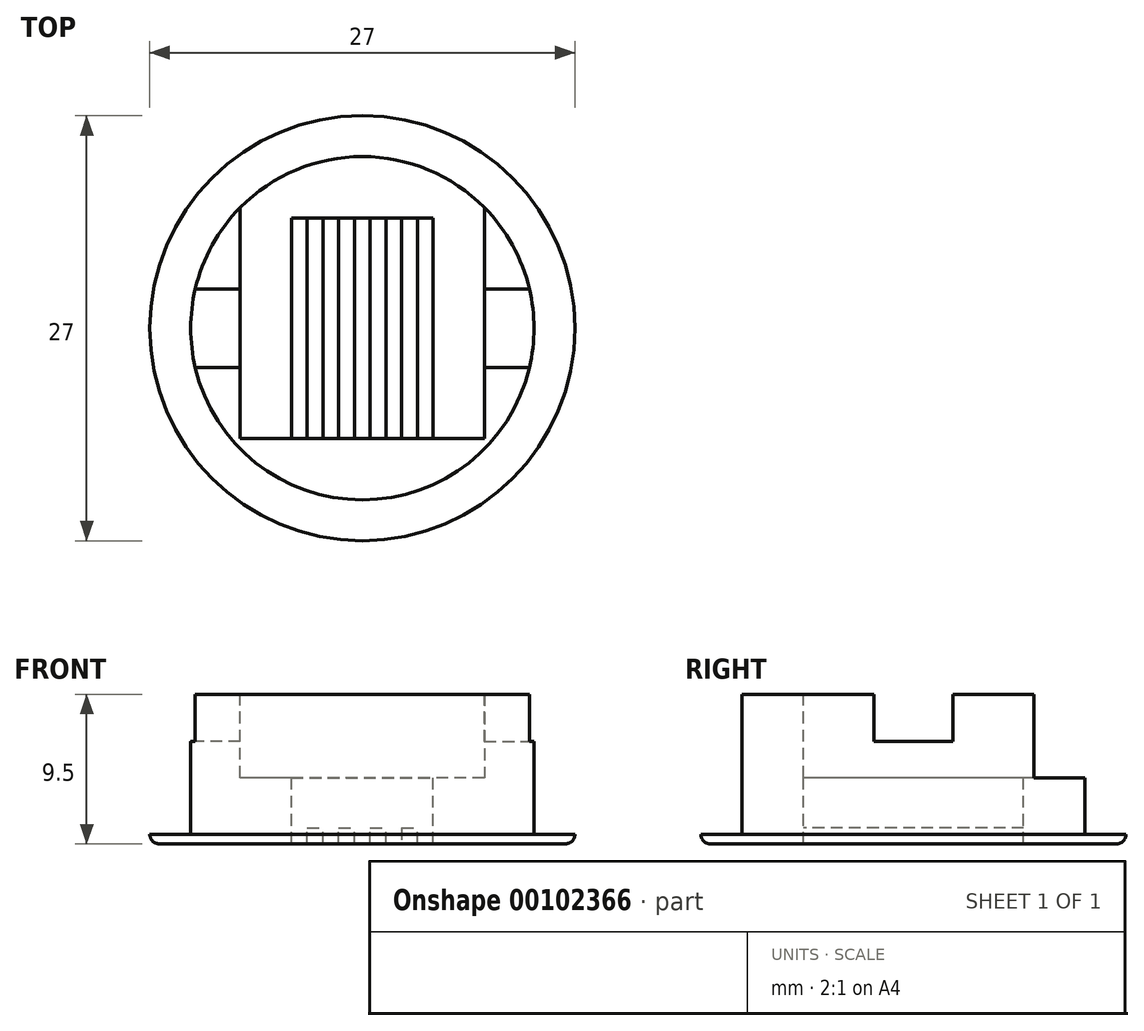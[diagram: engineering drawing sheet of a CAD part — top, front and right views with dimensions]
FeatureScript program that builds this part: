
annotation { "Feature Type Name" : "Feature", "Feature Type Description" : "" }
export const myFeature = defineFeature(function(context is Context, id is Id, definition is map)
    precondition{}
    {
        {
            var Q0;
            Q0=qCreatedBy(makeId("Top.planeOp"),FACE);
            var sketch = newSketch(context, id + "F0", { "sketchPlane" : qUnion([Q0])});
            skCircle(sketch, "E0", {"center": v(0, 0) * mm, "radius": 13.5 * mm});
            skSolve(sketch);
        }
        {
            var Q0;
            Q0=makeQuery(id+"F0.imprint","IMPRINT",FACE,{"disambiguationData":[TD([[makeQuery(id+"F0.imprint","IMPRINT",EDGE,{"derivedFrom":sQuery(id+"F0.wireOp",EDGE,"E0")}),1.0]])]});
            extrude(context, id + "F1", {"entities" : qUnion([Q0]), "depth" : 0.6 * mm});
        }
        {
            var Q0;
            Q0=makeQuery(id+"F1.opExtrude","CAP_EDGE",EDGE,{"disambiguationData":[OSD([sQuery(id+"F0.wireOp",EDGE,"E0")])],"isStart":true});
            fillet(context, id + "F2", {"entities" : qUnion([Q0]), "radius" : 0.6 * mm, "tangentPropagation" : true, "allowEdgeOverflow" : false});
        }
        {
            var Q0;
            Q0=qCreatedBy(makeId("Front.planeOp"),FACE);
            var sketch = newSketch(context, id + "F3", { "sketchPlane" : qUnion([Q0])});
            skLineSegment(sketch, "E1", {"start": v(0, 0) * mm, "end": v(0.5, 0) * mm});
            skLineSegment(sketch, "E2", {"start": v(0, 0) * mm, "end": v(-0.5, 0) * mm});
            skLineSegment(sketch, "E3", {"start": v(-0.5, 0) * mm, "end": v(-0.5, 1) * mm});
            skLineSegment(sketch, "E4", {"start": v(0.5, 0) * mm, "end": v(0.5, 1) * mm});
            skLineSegment(sketch, "E5", {"start": v(-1.5, 0) * mm, "end": v(-1.5, 1) * mm});
            skLineSegment(sketch, "E6", {"start": v(-1.5, 0) * mm, "end": v(-2.5, 0) * mm});
            skLineSegment(sketch, "E7", {"start": v(-3.5, 0) * mm, "end": v(-3.5, 1) * mm});
            skLineSegment(sketch, "E8", {"start": v(-3.5, 0) * mm, "end": v(-4.5, 0) * mm});
            skLineSegment(sketch, "E9", {"start": v(1.5, 0) * mm, "end": v(1.5, 1) * mm});
            skLineSegment(sketch, "E10", {"start": v(1.5, 0) * mm, "end": v(2.5, 0) * mm});
            skLineSegment(sketch, "E11", {"start": v(2.5, 0) * mm, "end": v(2.5, 1) * mm});
            skLineSegment(sketch, "E12", {"start": v(3.5, 0) * mm, "end": v(4.5, 0) * mm});
            skLineSegment(sketch, "E13", {"start": v(4.5, 0) * mm, "end": v(4.5, 4.2) * mm});
            skLineSegment(sketch, "E14", {"start": v(-4.5, 0) * mm, "end": v(-4.5, 4.2) * mm});
            skLineSegment(sketch, "E15", {"start": v(-2.5, 0) * mm, "end": v(-2.5, 1) * mm});
            skLineSegment(sketch, "E16", {"start": v(3.5, 0) * mm, "end": v(3.5, 1) * mm});
            skLineSegment(sketch, "E17", {"start": v(-4.5, 4.2) * mm, "end": v(4.5, 4.2) * mm});
            skLineSegment(sketch, "E18", {"start": v(-3.5, 1) * mm, "end": v(-2.5, 1) * mm});
            skLineSegment(sketch, "E19", {"start": v(-1.5, 1) * mm, "end": v(-0.5, 1) * mm});
            skLineSegment(sketch, "E20", {"start": v(0.5, 1) * mm, "end": v(1.5, 1) * mm});
            skLineSegment(sketch, "E21", {"start": v(2.5, 1) * mm, "end": v(3.5, 1) * mm});
            skSolve(sketch);
        }
        {
            var Q0;
            Q0=qCreatedBy(makeId("Front.planeOp"),FACE);
            var sketch = newSketch(context, id + "F4", { "sketchPlane" : qUnion([Q0])});
            skLineSegment(sketch, "E22", {"start": v(0, 0) * mm, "end": v(0.5, 0) * mm});
            skLineSegment(sketch, "E23", {"start": v(0, 0) * mm, "end": v(-0.5, 0) * mm});
            skLineSegment(sketch, "E24", {"start": v(-0.5, 0) * mm, "end": v(-0.5, 1) * mm});
            skLineSegment(sketch, "E25", {"start": v(0.5, 0) * mm, "end": v(0.5, 1) * mm});
            skLineSegment(sketch, "E26", {"start": v(-1.5, 0) * mm, "end": v(-1.5, 1) * mm});
            skLineSegment(sketch, "E27", {"start": v(-1.5, 0) * mm, "end": v(-2.5, 0) * mm});
            skLineSegment(sketch, "E28", {"start": v(-2.5, 0) * mm, "end": v(-2.5, 1) * mm});
            skLineSegment(sketch, "E29", {"start": v(-3.5, 0) * mm, "end": v(-3.5, 1) * mm});
            skLineSegment(sketch, "E30", {"start": v(-3.5, 0) * mm, "end": v(-4.5, 0) * mm});
            skLineSegment(sketch, "E31", {"start": v(-4.5, 0) * mm, "end": v(-4.5, 4.2) * mm});
            skLineSegment(sketch, "E32", {"start": v(1.5, 0) * mm, "end": v(1.5, 1) * mm});
            skLineSegment(sketch, "E33", {"start": v(1.5, 0) * mm, "end": v(2.5, 0) * mm});
            skLineSegment(sketch, "E34", {"start": v(3.5, 0) * mm, "end": v(3.5, 1) * mm});
            skLineSegment(sketch, "E35", {"start": v(3.5, 0) * mm, "end": v(4.5, 0) * mm});
            skLineSegment(sketch, "E36", {"start": v(4.5, 0) * mm, "end": v(4.5, 4.2) * mm});
            skLineSegment(sketch, "E37", {"start": v(-3.5, 1) * mm, "end": v(-2.5, 1) * mm});
            skLineSegment(sketch, "E38", {"start": v(-1.5, 1) * mm, "end": v(-0.5, 1) * mm});
            skLineSegment(sketch, "E39", {"start": v(0.5, 1) * mm, "end": v(1.5, 1) * mm});
            skLineSegment(sketch, "E40", {"start": v(2.5, 1) * mm, "end": v(3.5, 1) * mm});
            skLineSegment(sketch, "E41", {"start": v(4.5, 4.2) * mm, "end": v(-4.5, 4.2) * mm});
            skLineSegment(sketch, "E42", {"start": v(2.5, 1) * mm, "end": v(2.5, 0) * mm});
            skSolve(sketch);
        }
        {
            var Q0;
            Q0=makeQuery(id+"F1.opExtrude","CAP_FACE",FACE,{"disambiguationData":[OSD([sQuery(id+"F0.wireOp",EDGE,"E0")])],"isStart":false});
            var sketch = newSketch(context, id + "F5", { "sketchPlane" : qUnion([Q0])});
            skCircle(sketch, "E43", {"center": v(0, 0) * mm, "radius": 10.9 * mm});
            skSolve(sketch);
        }
        {
            var Q0;
            Q0=makeQuery(id+"F5.imprint","IMPRINT",FACE,{"disambiguationData":[TD([[makeQuery(id+"F5.imprint","IMPRINT",EDGE,{"derivedFrom":sQuery(id+"F5.wireOp",EDGE,"E43")}),1.0]])]});
            extrude(context, id + "F6", {"entities" : qUnion([Q0]), "operationType" : NewBodyOperationType.ADD, "depth" : 8.9 * mm});
        }
        {
            var Q0;
            Q0=qCreatedBy(makeId("Front.planeOp"),FACE);
            var sketch = newSketch(context, id + "F7", { "sketchPlane" : qUnion([Q0])});
            skLineSegment(sketch, "E44", {"start": v(0, 0) * mm, "end": v(0, 4.2) * mm});
            skLineSegment(sketch, "E45", {"start": v(0, 4.2) * mm, "end": v(7.75, 4.2) * mm});
            skLineSegment(sketch, "E46", {"start": v(0, 4.2) * mm, "end": v(-7.75, 4.2) * mm});
            skLineSegment(sketch, "E47", {"start": v(-7.75, 4.2) * mm, "end": v(-7.75, 9.5) * mm});
            skLineSegment(sketch, "E48", {"start": v(7.75, 4.2) * mm, "end": v(7.75, 9.5) * mm});
            skLineSegment(sketch, "E49", {"start": v(-7.75, 9.5) * mm, "end": v(7.75, 9.5) * mm});
            skSolve(sketch);
        }
        {
            var Q0;
            Q0=qCreatedBy(makeId("Front.planeOp"),FACE);
            var sketch = newSketch(context, id + "F8", { "sketchPlane" : qUnion([Q0])});
            skLineSegment(sketch, "E50", {"start": v(0, 0) * mm, "end": v(0, 4.2) * mm});
            skLineSegment(sketch, "E51", {"start": v(0, 4.2) * mm, "end": v(7.75, 4.2) * mm});
            skLineSegment(sketch, "E52", {"start": v(0, 4.2) * mm, "end": v(-7.75, 4.2) * mm});
            skLineSegment(sketch, "E53", {"start": v(7.75, 4.2) * mm, "end": v(7.75, 9.5) * mm});
            skLineSegment(sketch, "E54", {"start": v(-7.75, 4.2) * mm, "end": v(-7.75, 9.5) * mm});
            skLineSegment(sketch, "E55", {"start": v(-7.75, 9.5) * mm, "end": v(7.75, 9.5) * mm});
            skSolve(sketch);
        }
        {
            var Q0;
            Q0 = qSketchRegion(id + "F3", true);
            extrude(context, id + "F9", {"entities" : qUnion([Q0]), "operationType" : NewBodyOperationType.REMOVE, "oppositeDirection" : true, "depth" : 7 * mm});
        }
        {
            var Q0;
            Q0 = qSketchRegion(id + "F4", true);
            extrude(context, id + "F10", {"entities" : qUnion([Q0]), "operationType" : NewBodyOperationType.REMOVE, "depth" : 7 * mm});
        }
        {
            var Q0;
            Q0 = qSketchRegion(id + "F7", true);
            extrude(context, id + "F11", {"entities" : qUnion([Q0]), "operationType" : NewBodyOperationType.REMOVE, "oppositeDirection" : true, "depth" : 25 * mm});
        }
        {
            var Q0;
            Q0 = qSketchRegion(id + "F8", true);
            extrude(context, id + "F12", {"entities" : qUnion([Q0]), "operationType" : NewBodyOperationType.REMOVE, "depth" : 7 * mm});
        }
        {
            var Q0;
            Q0=makeQuery(id+"F6.opExtrude","CAP_FACE",FACE,{"disambiguationData":[OSD([sQuery(id+"F5.wireOp",EDGE,"E43")])],"isStart":false});
            var sketch = newSketch(context, id + "F13", { "sketchPlane" : qUnion([Q0])});
            skLineSegment(sketch, "E56", {"start": v(0, 0) * mm, "end": v(7.75, 0) * mm});
            skLineSegment(sketch, "E57", {"start": v(0, 0) * mm, "end": v(-7.75, 0) * mm});
            skLineSegment(sketch, "E58", {"start": v(7.75, 0) * mm, "end": v(7.75, 2.5) * mm});
            skLineSegment(sketch, "E59", {"start": v(7.75, 0) * mm, "end": v(7.75, -2.5) * mm});
            skLineSegment(sketch, "E60", {"start": v(7.75, -2.5) * mm, "end": v(11.75, -2.5) * mm});
            skLineSegment(sketch, "E61", {"start": v(7.75, 2.5) * mm, "end": v(11.75, 2.5) * mm});
            skLineSegment(sketch, "E62", {"start": v(-7.75, 0) * mm, "end": v(-7.75, 2.5) * mm});
            skLineSegment(sketch, "E63", {"start": v(-7.75, 2.5) * mm, "end": v(-11.75, 2.5) * mm});
            skLineSegment(sketch, "E64", {"start": v(-7.75, 0) * mm, "end": v(-7.75, -2.5) * mm});
            skLineSegment(sketch, "E65", {"start": v(-7.75, -2.5) * mm, "end": v(-11.75, -2.5) * mm});
            skLineSegment(sketch, "E66", {"start": v(-11.75, 2.5) * mm, "end": v(-11.75, -2.5) * mm});
            skLineSegment(sketch, "E67", {"start": v(11.75, 2.5) * mm, "end": v(11.75, -2.5) * mm});
            skSolve(sketch);
        }
        {
            var Q0;
            {var subQ6=sQuery(id+"F13.wireOp",EDGE,"E62");Q0=makeQuery(id+"F13.imprint","IMPRINT",FACE,{"disambiguationData":[TD([[makeQuery(id+"F13.imprint","IMPRINT",EDGE,{"derivedFrom":subQ6}),-1.0]])]});}
            var Q1;
            {var subQ1=sQuery(id+"F13.wireOp",EDGE,"E58");Q1=makeQuery(id+"F13.imprint","IMPRINT",FACE,{"disambiguationData":[TD([[makeQuery(id+"F13.imprint","IMPRINT",EDGE,{"derivedFrom":subQ1}),1.0]])]});}
            extrude(context, id + "F14", {"entities" : qUnion([Q0, Q1]), "operationType" : NewBodyOperationType.REMOVE, "oppositeDirection" : true, "depth" : 3 * mm});
        }
    });
